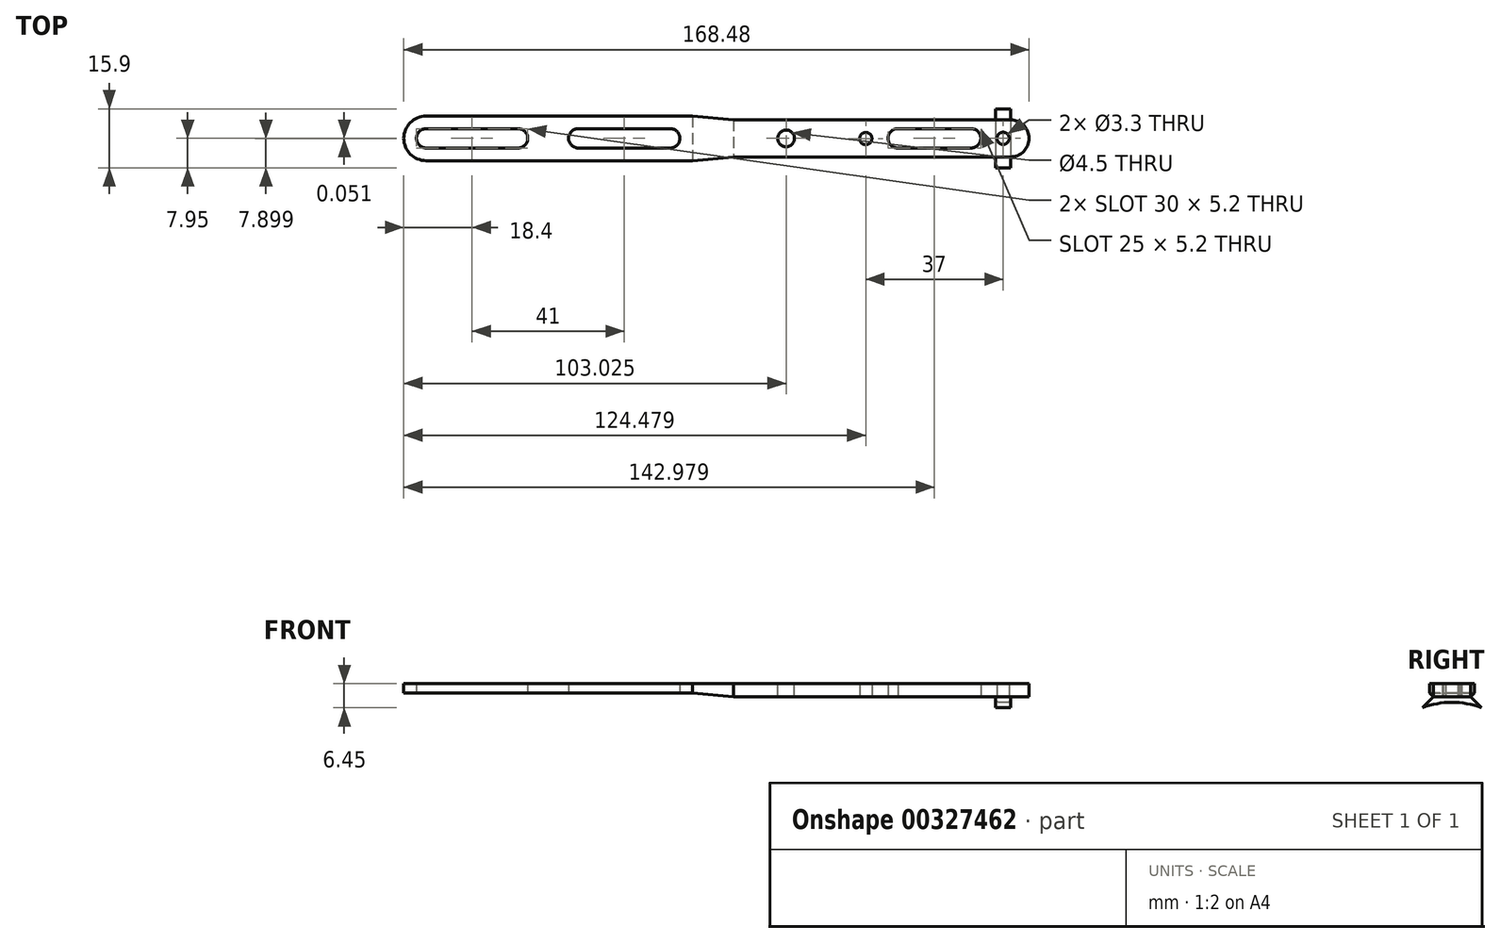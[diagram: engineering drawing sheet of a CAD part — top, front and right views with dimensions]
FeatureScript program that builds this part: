
annotation { "Feature Type Name" : "Feature", "Feature Type Description" : "" }
export const myFeature = defineFeature(function(context is Context, id is Id, definition is map)
    precondition{}
    {
        {
            var Q0;
            Q0=qCreatedBy(makeId("Top.planeOp"),FACE);
            var sketch = newSketch(context, id + "F0", { "sketchPlane" : qUnion([Q0])});
            skCircle(sketch, "E0", {"center": v(46.68, -0.05) * mm, "radius": 1.65 * mm});
            skCircle(sketch, "E1", {"center": v(83.68, 0) * mm, "radius": 1.65 * mm});
            skLineSegment(sketch, "E2", {"start": v(-104.54, 0) * mm, "end": v(102.54, 0) * mm, "construction": true});
            skArc(sketch, "E3", {"start": v(-71.8, 6) * mm, "mid": v(-77.8, 0) * mm, "end": v(-71.8, -6) * mm});
            skArc(sketch, "E4", {"start": v(-71.8, 2.6) * mm, "mid": v(-74.4, 0) * mm, "end": v(-71.8, -2.6) * mm});
            skArc(sketch, "E5", {"start": v(-47, -2.6) * mm, "mid": v(-44.4, 0) * mm, "end": v(-47, 2.6) * mm});
            skArc(sketch, "E6", {"start": v(-30.8, 2.6) * mm, "mid": v(-33.4, 0) * mm, "end": v(-30.8, -2.6) * mm});
            skArc(sketch, "E7", {"start": v(-6, -2.6) * mm, "mid": v(-3.4, 0) * mm, "end": v(-6, 2.6) * mm});
            skArc(sketch, "E8", {"start": v(85.68, -5) * mm, "mid": v(90.68, 0) * mm, "end": v(85.68, 5) * mm});
            skLineSegment(sketch, "E9", {"start": v(-71.8, 2.6) * mm, "end": v(-47, 2.6) * mm});
            skLineSegment(sketch, "E10", {"start": v(-71.8, -2.6) * mm, "end": v(-47, -2.6) * mm});
            skArc(sketch, "E11", {"start": v(75.08, -2.6) * mm, "mid": v(77.68, 0) * mm, "end": v(75.08, 2.6) * mm});
            skArc(sketch, "E12", {"start": v(55.32, 2.6) * mm, "mid": v(52.68, 0.01) * mm, "end": v(55.3, -2.6) * mm});
            skLineSegment(sketch, "E13", {"start": v(55.32, 2.6) * mm, "end": v(75.08, 2.6) * mm});
            skLineSegment(sketch, "E14", {"start": v(55.27, -2.6) * mm, "end": v(75.08, -2.6) * mm});
            skLineSegment(sketch, "E15.trimOffspring", {"start": v(-30.8, 2.6) * mm, "end": v(-6, 2.6) * mm});
            skLineSegment(sketch, "E16.trimOffspring", {"start": v(-30.8, -2.6) * mm, "end": v(-6, -2.6) * mm});
            skLineSegment(sketch, "E17", {"start": v(11, 5) * mm, "end": v(85.68, 5) * mm});
            skLineSegment(sketch, "E18", {"start": v(11, -5) * mm, "end": v(85.68, -5) * mm});
            skLineSegment(sketch, "E19", {"start": v(-12.18, 6) * mm, "end": v(-12.18, 6) * mm});
            skLineSegment(sketch, "E20", {"start": v(-71.8, 6) * mm, "end": v(0, 6) * mm});
            skLineSegment(sketch, "E21", {"start": v(-71.8, -6) * mm, "end": v(0, -6) * mm});
            skLineSegment(sketch, "E22", {"start": v(0, -6) * mm, "end": v(11, -5) * mm});
            skLineSegment(sketch, "E23", {"start": v(0, 6) * mm, "end": v(11, 5) * mm});
            skLineSegment(sketch, "E24", {"start": v(11, -10.94) * mm, "end": v(11, 10.77) * mm, "construction": true});
            skSolve(sketch);
        }
        {
            var Q0;
            Q0=makeQuery(id+"F0.imprint","IMPRINT",FACE,{"disambiguationData":[TD([[makeQuery(id+"F0.imprint","IMPRINT",EDGE,{"derivedFrom":sQuery(id+"F0.wireOp",EDGE,"E0")}),-1.0]])]});
            extrude(context, id + "F1", {"entities" : qUnion([Q0]), "depth" : 3.5 * mm});
        }
        {
            var Q0;
            Q0=qCreatedBy(makeId("Front.planeOp"),FACE);
            var sketch = newSketch(context, id + "F2", { "sketchPlane" : qUnion([Q0])});
            skLineSegment(sketch, "E25", {"start": v(-80.44, 0) * mm, "end": v(-80.44, 1) * mm});
            skLineSegment(sketch, "E26", {"start": v(-80.44, 1) * mm, "end": v(0, 1) * mm});
            skLineSegment(sketch, "E27", {"start": v(0, 1) * mm, "end": v(11, 0) * mm});
            skLineSegment(sketch, "E28", {"start": v(11, 0) * mm, "end": v(-80.44, 0) * mm});
            skSolve(sketch);
        }
        {
            var Q0;
            Q0=qSketchRegion(id+"F2",true);
            extrude(context, id + "F3", {"entities" : qUnion([Q0]), "operationType" : NewBodyOperationType.REMOVE, "endBound" : BoundingType.SYMMETRIC, "oppositeDirection" : true, "depth" : 12 * mm});
        }
        {
            var Q0;
            Q0=makeQuery(id+"F1.opExtrude","CAP_EDGE",EDGE,{"disambiguationData":[OSD([sQuery(id+"F0.wireOp",EDGE,"E1")])],"isStart":true});
            cPlane(context, id + "F4", {"entities" : qUnion([Q0]), "cplaneType" : CPlaneType.LINE_ANGLE, "offset" : 25 * mm, "angle" : 360 * degree, "width" : 150 * mm, "height" : 150 * mm});
        }
        {
            var Q0;
            Q0=qCreatedBy(id+"F4.planeOp",FACE);
            var sketch = newSketch(context, id + "F5", { "sketchPlane" : qUnion([Q0])});
            skArc(sketch, "E29", {"start": v(7.95, -2.95) * mm, "mid": v(0, -1.5) * mm, "end": v(-7.95, -2.95) * mm});
            skLineSegment(sketch, "E30", {"start": v(5, 0) * mm, "end": v(7.95, -2.95) * mm});
            skLineSegment(sketch, "E31.MirrorCS", {"start": v(-5, 0) * mm, "end": v(-7.95, -2.95) * mm});
            skLineSegment(sketch, "E32", {"start": v(5.75, -0.75) * mm, "end": v(-5.75, -0.75) * mm});
            skLineSegment(sketch, "E33", {"start": v(5, 0) * mm, "end": v(-5, 0) * mm});
            skSolve(sketch);
        }
        {
            var Q0;
            {var subQ2=sQuery(id+"F5.wireOp",EDGE,"E32");Q0=makeQuery(id+"F5.imprint","IMPRINT",FACE,{"disambiguationData":[TD([[makeQuery(id+"F5.imprint","IMPRINT",EDGE,{"derivedFrom":subQ2}),-1.0]])]});}
            var Q1;
            {var subQ0=sQuery(id+"F5.wireOp",EDGE,"E29");Q1=makeQuery(id+"F5.imprint","IMPRINT",FACE,{"disambiguationData":[TD([[makeQuery(id+"F5.imprint","IMPRINT",EDGE,{"derivedFrom":subQ0}),-1.0]])]});}
            extrude(context, id + "F6", {"entities" : qUnion([Q0, Q1]), "operationType" : NewBodyOperationType.ADD, "endBound" : BoundingType.SYMMETRIC, "depth" : 4 * mm});
        }
        {
            var Q0;
            Q0=makeQuery(id+"F1.opExtrude","CAP_EDGE",EDGE,{"disambiguationData":[OSD([sQuery(id+"F0.wireOp",EDGE,"E0")])],"isStart":true});
            cPlane(context, id + "F7", {"entities" : qUnion([Q0]), "cplaneType" : CPlaneType.LINE_ANGLE, "offset" : 25 * mm, "angle" : 0 * degree, "width" : 150 * mm, "height" : 150 * mm});
        }
        {
            var Q0;
            Q0=qCreatedBy(id+"F7.planeOp",FACE);
            var sketch = newSketch(context, id + "F8", { "sketchPlane" : qUnion([Q0])});
            skArc(sketch, "E34", {"start": v(7.95, -2.95) * mm, "mid": v(0, -1.5) * mm, "end": v(-7.95, -2.95) * mm});
            skLineSegment(sketch, "E35", {"start": v(5, 0) * mm, "end": v(7.95, -2.95) * mm});
            skLineSegment(sketch, "E36.MirrorCS", {"start": v(-5, 0) * mm, "end": v(-7.95, -2.95) * mm});
            skLineSegment(sketch, "E37", {"start": v(5.75, -0.75) * mm, "end": v(-5.75, -0.75) * mm});
            skLineSegment(sketch, "E38", {"start": v(5, 0) * mm, "end": v(-5, 0) * mm});
            skSolve(sketch);
        }
        {
            var Q0;
            Q0=makeQuery(id+"FjXZQur7R7jTskj_1.opExtrude","SWEPT_FACE",FACE,{"disambiguationData":[OSD([sQuery(id+"F8.wireOp",EDGE,"E38")])]});
            var Q1;
            Q1=makeQuery(id+"F6.opExtrude","SWEPT_FACE",FACE,{"disambiguationData":[OSD([sQuery(id+"F5.wireOp",EDGE,"E33")])]});
            extrude(context, id + "F9", {"entities" : qUnion([Q0, Q1]), "operationType" : NewBodyOperationType.REMOVE, "oppositeDirection" : true, "depth" : 1.75 * mm});
        }
        {
            var Q0;
            Q0=makeQuery(id+"F1.opExtrude","CAP_FACE",FACE,{"disambiguationData":[OSD([sQuery(id+"F0.wireOp",EDGE,"E0"),sQuery(id+"F0.wireOp",EDGE,"E1"),sQuery(id+"F0.wireOp",EDGE,"E3"),sQuery(id+"F0.wireOp",EDGE,"E4"),sQuery(id+"F0.wireOp",EDGE,"E5"),sQuery(id+"F0.wireOp",EDGE,"E6"),sQuery(id+"F0.wireOp",EDGE,"E7"),sQuery(id+"F0.wireOp",EDGE,"E8"),sQuery(id+"F0.wireOp",EDGE,"E9"),sQuery(id+"F0.wireOp",EDGE,"E10"),sQuery(id+"F0.wireOp",EDGE,"E11"),sQuery(id+"F0.wireOp",EDGE,"E12"),sQuery(id+"F0.wireOp",EDGE,"E13"),sQuery(id+"F0.wireOp",EDGE,"E14"),sQuery(id+"F0.wireOp",EDGE,"E15.trimOffspring"),sQuery(id+"F0.wireOp",EDGE,"E16.trimOffspring"),sQuery(id+"F0.wireOp",EDGE,"E17"),sQuery(id+"F0.wireOp",EDGE,"E18"),sQuery(id+"F0.wireOp",EDGE,"E20"),sQuery(id+"F0.wireOp",EDGE,"E21"),sQuery(id+"F0.wireOp",EDGE,"E22"),sQuery(id+"F0.wireOp",EDGE,"E23")])],"isStart":false});
            var sketch = newSketch(context, id + "F10", { "sketchPlane" : qUnion([Q0])});
            skPoint(sketch, "E39", {"position": v(25.22, 0) * mm});
            skSolve(sketch);
        }
        {
            var Q0;
            Q0=sQuery(id+"F10.wireOp",VERTEX,"E39");
            var Q1;
            Q1=makeQuery(id+"F1.opExtrude","SWEPT_BODY",BODY,{"disambiguationData":[OSD([sQuery(id+"F0.wireOp",EDGE,"E0"),sQuery(id+"F0.wireOp",EDGE,"E1"),sQuery(id+"F0.wireOp",EDGE,"E3"),sQuery(id+"F0.wireOp",EDGE,"E4"),sQuery(id+"F0.wireOp",EDGE,"E5"),sQuery(id+"F0.wireOp",EDGE,"E6"),sQuery(id+"F0.wireOp",EDGE,"E7"),sQuery(id+"F0.wireOp",EDGE,"E8"),sQuery(id+"F0.wireOp",EDGE,"E9"),sQuery(id+"F0.wireOp",EDGE,"E10"),sQuery(id+"F0.wireOp",EDGE,"E11"),sQuery(id+"F0.wireOp",EDGE,"E12"),sQuery(id+"F0.wireOp",EDGE,"E13"),sQuery(id+"F0.wireOp",EDGE,"E14"),sQuery(id+"F0.wireOp",EDGE,"E15.trimOffspring"),sQuery(id+"F0.wireOp",EDGE,"E16.trimOffspring"),sQuery(id+"F0.wireOp",EDGE,"E17"),sQuery(id+"F0.wireOp",EDGE,"E18"),sQuery(id+"F0.wireOp",EDGE,"E20"),sQuery(id+"F0.wireOp",EDGE,"E21"),sQuery(id+"F0.wireOp",EDGE,"E22"),sQuery(id+"F0.wireOp",EDGE,"E23")])]});
            hole(context, id + "F11", {"style" : HoleStyle.SIMPLE, "endStyle" : HoleEndStyle.BLIND, "standardTappedOrClearance" : lookupTablePath({ "standard" : "ISO", "engagement" : "50%", "pitch" : "0.8 mm", "size" : "M5", "type" : "Tapped" }), "standardBlindInLast" : lookupTablePath({ "standard" : "ISO", "fit" : "Normal", "engagement" : "50%", "pitch" : "0.8 mm", "size" : "M5", "type" : "Clearance & tapped" }), "holeDiameter" : 4.5 * mm, "majorDiameter" : 5 * mm, "showTappedDepth" : true, "holeDepth" : 52.4 * mm, "tappedDepth" : 50 * mm, "tapClearance" : 3, "locations" : qUnion([Q0]), "scope" : qUnion([Q1])});
        }
    });
